annotation { "Feature Type Name" : "Feature", "Feature Type Description" : "" }
export const myFeature = defineFeature(function(context is Context, id is Id, definition is map)
    precondition{}
    {
        {
            var Q0;
            Q0=qCreatedBy(makeId("Front.planeOp"),FACE);
            var sketch = newSketch(context, id + "F0", { "sketchPlane" : qUnion([Q0])});
            skLineSegment(sketch, "E0", {"start": v(-64.1, -46.27) * mm, "end": v(65.9, -46.27) * mm});
            skLineSegment(sketch, "E1", {"start": v(-64.1, -46.27) * mm, "end": v(-64.1, -16.27) * mm});
            skLineSegment(sketch, "E2", {"start": v(-64.1, -46.27) * mm, "end": v(-60.1, -46.27) * mm});
            skLineSegment(sketch, "E3", {"start": v(-60.1, -46.27) * mm, "end": v(-60.1, -16.27) * mm});
            skLineSegment(sketch, "E4", {"start": v(-60.1, -46.27) * mm, "end": v(-53.1, -46.27) * mm});
            skLineSegment(sketch, "E5", {"start": v(-53.1, -46.27) * mm, "end": v(-53.1, -16.27) * mm});
            skLineSegment(sketch, "E6", {"start": v(-49.1, -46.32) * mm, "end": v(-49.1, -16.32) * mm});
            skLineSegment(sketch, "E7", {"start": v(-53.1, -46.32) * mm, "end": v(-49.1, -46.32) * mm});
            skLineSegment(sketch, "E8", {"start": v(-49.1, -46.32) * mm, "end": v(-38.47, -46.27) * mm});
            skLineSegment(sketch, "E9", {"start": v(-38.47, -46.27) * mm, "end": v(-38.89, 32.17) * mm, "construction": true});
            skLineSegment(sketch, "E10", {"start": v(-64.1, -16.27) * mm, "end": v(-60.1, -16.27) * mm});
            skLineSegment(sketch, "E11", {"start": v(-53.1, -16.27) * mm, "end": v(-49.1, -16.32) * mm});
            skLineSegment(sketch, "E12", {"start": v(-68.63, -16.25) * mm, "end": v(-38.63, -16.25) * mm});
            skLineSegment(sketch, "E13", {"start": v(-68.63, -14.09) * mm, "end": v(-38.63, -14.09) * mm});
            skArc(sketch, "E14", {"start": v(-68.63, -14.09) * mm, "mid": v(-69.7, -15.17) * mm, "end": v(-68.63, -16.25) * mm});
            skLineSegment(sketch, "E15", {"start": v(-38.63, -14.09) * mm, "end": v(-38.68, -4.09) * mm});
            skPoint(sketch, "E15.endSnap0", {"position": v(-38.68, -7.05) * mm});
            skLineSegment(sketch, "E16", {"start": v(-38.68, -4.09) * mm, "end": v(-52.68, -4.16) * mm});
            skFitSpline(sketch, "E17", {"points": [v(-52.68, -4.16) * mm, v(-58.68, -8.88) * mm, v(-69.52, -10.67) * mm, v(-80.9, -8.11) * mm, v(-80.17, -8.88) * mm, v(-72.59, -13.73) * mm, v(-68.63, -14.09) * mm], "startDerivative": vector(-32.22, -24.94) * mm, "endDerivative": vector(26.6, -3.14) * mm});
            skLineSegment(sketch, "E18", {"start": v(-38.76, 7.91) * mm, "end": v(-58.76, 7.77) * mm});
            skLineSegment(sketch, "E19", {"start": v(-58.76, 7.77) * mm, "end": v(-52.68, -4.16) * mm});
            skLineSegment(sketch, "E20", {"start": v(-38.76, 7.91) * mm, "end": v(-38.74, 4.91) * mm});
            skLineSegment(sketch, "E21", {"start": v(-38.76, 7.91) * mm, "end": v(-38.9, 32.91) * mm});
            skFitSpline(sketch, "E22", {"points": [v(-38.9, 32.91) * mm, v(-40.61, 19.74) * mm, v(-42.06, 14.37) * mm, v(-43.86, 12.97) * mm, v(-53.8, 12.33) * mm, v(-64.1, 13.48) * mm, v(-69.15, 16.29) * mm, v(-67.17, 13.48) * mm, v(-63.55, 9.39) * mm, v(-58.76, 7.77) * mm], "startDerivative": vector(-10.23, -89.2) * mm, "endDerivative": vector(52.36, -10.93) * mm});
            skPoint(sketch, "E23", {"position": v(-55.8, -6.79) * mm});
            skFitSpline(sketch, "E24", {"points": [v(-55.8, -6.79) * mm, v(-59.58, -4.66) * mm, v(-60.84, -3.51) * mm, v(-58.68, -8.88) * mm], "startDerivative": vector(-11.5, 5.17) * mm, "endDerivative": vector(8.54, -18.92) * mm});
            skPoint(sketch, "E25", {"position": v(-46.92, 12.53) * mm});
            skPoint(sketch, "E26", {"position": v(-51.81, 12.36) * mm});
            skFitSpline(sketch, "E27", {"points": [v(-46.92, 12.53) * mm, v(-50.19, 15.14) * mm, v(-52.72, 17.82) * mm, v(-51.81, 12.36) * mm], "startDerivative": vector(-9.9, 6.4) * mm, "endDerivative": vector(5.44, -21.54) * mm});
            skLineSegment(sketch, "E28.MirrorCS", {"start": v(-23.84, -46.11) * mm, "end": v(-24.16, -16.11) * mm});
            skLineSegment(sketch, "E29.MirrorCS", {"start": v(-27.83, -46.2) * mm, "end": v(-28.15, -16.21) * mm});
            skLineSegment(sketch, "E30.MirrorCS", {"start": v(-16.84, -46.04) * mm, "end": v(-17.16, -16.04) * mm});
            skLineSegment(sketch, "E31.MirrorCS", {"start": v(-12.84, -46) * mm, "end": v(-13.16, -16) * mm});
            skLineSegment(sketch, "E32.MirrorCS", {"start": v(-23.83, -46.17) * mm, "end": v(-27.83, -46.2) * mm});
            skLineSegment(sketch, "E33.MirrorCS", {"start": v(-8.63, -15.93) * mm, "end": v(-38.63, -16.25) * mm});
            skLineSegment(sketch, "E34.MirrorCS", {"start": v(-8.66, -13.77) * mm, "end": v(-38.66, -14.09) * mm});
            skArc(sketch, "E35.MirrorCS", {"start": v(-8.66, -13.77) * mm, "mid": v(-7.57, -14.83) * mm, "end": v(-8.63, -15.93) * mm});
            skFitSpline(sketch, "E36.MirrorCS", {"points": [v(-24.71, -4.01) * mm, v(-18.66, -8.66) * mm, v(-7.8, -10.34) * mm, v(3.55, -7.66) * mm, v(2.83, -8.43) * mm, v(-4.7, -13.37) * mm, v(-8.66, -13.77) * mm], "startDerivative": vector(32.49, -24.6) * mm, "endDerivative": vector(-26.56, -3.42) * mm});
            skFitSpline(sketch, "E37.MirrorCS", {"points": [v(-21.57, -6.6) * mm, v(-17.8, -4.44) * mm, v(-16.55, -3.28) * mm, v(-18.66, -8.66) * mm], "startDerivative": vector(11.44, 5.29) * mm, "endDerivative": vector(-8.33, -19.01) * mm});
            skLineSegment(sketch, "E38.MirrorCS", {"start": v(-38.71, -4.09) * mm, "end": v(-24.71, -4.01) * mm});
            skLineSegment(sketch, "E39.MirrorCS", {"start": v(-18.76, 7.98) * mm, "end": v(-24.71, -4.01) * mm});
            skLineSegment(sketch, "E40.MirrorCS", {"start": v(-38.76, 7.91) * mm, "end": v(-18.76, 7.98) * mm});
            skFitSpline(sketch, "E41.MirrorCS", {"points": [v(-38.9, 32.91) * mm, v(-37.03, 19.75) * mm, v(-35.53, 14.4) * mm, v(-33.7, 13.02) * mm, v(-23.77, 12.49) * mm, v(-13.48, 13.75) * mm, v(-8.46, 16.61) * mm, v(-10.41, 13.78) * mm, v(-13.98, 9.65) * mm, v(-18.76, 7.98) * mm], "startDerivative": vector(11.19, -89.08) * mm, "endDerivative": vector(-52.24, -11.49) * mm});
            skFitSpline(sketch, "E42.MirrorCS", {"points": [v(-30.64, 12.62) * mm, v(-27.4, 15.26) * mm, v(-24.9, 17.97) * mm, v(-25.76, 12.5) * mm], "startDerivative": vector(9.83, 6.51) * mm, "endDerivative": vector(-5.2, -21.6) * mm});
            skLineSegment(sketch, "E43", {"start": v(-16.84, -46.04) * mm, "end": v(-12.84, -46) * mm});
            skLineSegment(sketch, "E44", {"start": v(-16.77, -16.03) * mm, "end": v(-13.16, -16) * mm});
            skLineSegment(sketch, "E45", {"start": v(-28.15, -16.21) * mm, "end": v(-24.16, -16.11) * mm});
            skLineSegment(sketch, "E46", {"start": v(-27.83, -46.2) * mm, "end": v(-23.83, -46.17) * mm});
            skLineSegment(sketch, "E47", {"start": v(-23.83, -46.17) * mm, "end": v(-24.16, -16.11) * mm});
            skLineSegment(sketch, "E48", {"start": v(-28.15, -16.21) * mm, "end": v(-27.83, -46.2) * mm});
            skLineSegment(sketch, "E49", {"start": v(-13.16, -16) * mm, "end": v(-12.84, -46) * mm});
            skLineSegment(sketch, "E50", {"start": v(-16.77, -16.03) * mm, "end": v(-16.84, -46.04) * mm});
            skSolve(sketch);
        }
        {
            var Q0;
            {var subQ5=sQuery(id+"F0.wireOp",EDGE,"E18");Q0=makeQuery(id+"F0.imprint","IMPRINT",FACE,{"disambiguationData":[TD([[makeQuery(id+"F0.imprint","IMPRINT",EDGE,{"derivedFrom":subQ5}),-1.0]])]});}
            var Q1;
            {var subQ0=sQuery(id+"F0.wireOp",EDGE,"E27");Q1=makeQuery(id+"F0.imprint","IMPRINT",FACE,{"disambiguationData":[TD([[makeQuery(id+"F0.imprint","IMPRINT",EDGE,{"derivedFrom":subQ0}),1.0]])]});}
            var Q2;
            {var subQ4=sQuery(id+"F0.wireOp",EDGE,"E21");Q2=makeQuery(id+"F0.imprint","IMPRINT",FACE,{"disambiguationData":[TD([[makeQuery(id+"F0.imprint","IMPRINT",EDGE,{"derivedFrom":subQ4}),-1.0]])]});}
            var Q3;
            {var subQ0=sQuery(id+"F0.wireOp",EDGE,"E42.MirrorCS");Q3=makeQuery(id+"F0.imprint","IMPRINT",FACE,{"disambiguationData":[TD([[makeQuery(id+"F0.imprint","IMPRINT",EDGE,{"derivedFrom":subQ0}),-1.0]])]});}
            var Q4;
            Q4=makeQuery(id+"F0.imprint","IMPRINT",FACE,{"disambiguationData":[TD([[makeQuery(id+"F0.imprint","IMPRINT",EDGE,{"derivedFrom":sQuery(id+"F0.wireOp",EDGE,"E12")}),1.0]])]});
            var Q5;
            {var subQ0=sQuery(id+"F0.wireOp",EDGE,"E37.MirrorCS");var subQ1=sQuery(id+"F0.wireOp",EDGE,"E36.MirrorCS");var subQ2=makeQuery(id+"F0.imprint","INTERSECT",VERTEX,{"disambiguationData":[OD(0.0)],"derivedFrom":[subQ1,subQ0]});Q5=makeQuery(id+"F0.imprint","IMPRINT",FACE,{"disambiguationData":[TD([[makeQuery(id+"F0.imprint","IMPRINT",EDGE,{"disambiguationData":[TD([[subQ2,-1.0]])],"derivedFrom":subQ1}),-1.0]])]});}
            var Q6;
            {var subQ1=sQuery(id+"F0.wireOp",EDGE,"E16");Q6=makeQuery(id+"F0.imprint","IMPRINT",FACE,{"disambiguationData":[TD([[makeQuery(id+"F0.imprint","IMPRINT",EDGE,{"derivedFrom":subQ1}),1.0]])]});}
            var Q7;
            {var subQ0=sQuery(id+"F0.wireOp",EDGE,"E24");Q7=makeQuery(id+"F0.imprint","IMPRINT",FACE,{"disambiguationData":[TD([[makeQuery(id+"F0.imprint","IMPRINT",EDGE,{"derivedFrom":subQ0}),1.0]])]});}
            var Q8;
            {var subQ0=sQuery(id+"F0.wireOp",EDGE,"E37.MirrorCS");Q8=makeQuery(id+"F0.imprint","IMPRINT",FACE,{"disambiguationData":[TD([[makeQuery(id+"F0.imprint","IMPRINT",EDGE,{"derivedFrom":subQ0}),-1.0]])]});}
            var Q9;
            Q9=makeQuery(id+"F0.imprint","IMPRINT",FACE,{"disambiguationData":[TD([[makeQuery(id+"F0.imprint","IMPRINT",EDGE,{"derivedFrom":sQuery(id+"F0.wireOp",EDGE,"E16")}),-1.0]])]});
            var Q10;
            Q10=makeQuery(id+"F0.imprint","IMPRINT",FACE,{"disambiguationData":[TD([[makeQuery(id+"F0.imprint","IMPRINT",EDGE,{"derivedFrom":sQuery(id+"F0.wireOp",EDGE,"E1")}),-1.0]])]});
            var Q11;
            {var subQ0=sQuery(id+"F0.wireOp",EDGE,"E5");Q11=makeQuery(id+"F0.imprint","IMPRINT",FACE,{"disambiguationData":[TD([[makeQuery(id+"F0.imprint","IMPRINT",EDGE,{"derivedFrom":subQ0}),-1.0]])]});}
            var Q12;
            Q12=makeQuery(id+"F0.imprint","IMPRINT",FACE,{"disambiguationData":[TD([[makeQuery(id+"F0.imprint","IMPRINT",EDGE,{"derivedFrom":sQuery(id+"F0.wireOp",EDGE,"E45")}),-1.0]])]});
            var Q13;
            Q13=makeQuery(id+"F0.imprint","IMPRINT",FACE,{"disambiguationData":[TD([[makeQuery(id+"F0.imprint","IMPRINT",EDGE,{"derivedFrom":sQuery(id+"F0.wireOp",EDGE,"E43")}),1.0]])]});
            extrude(context, id + "F1", {"entities" : qUnion([Q0, Q1, Q2, Q3, Q4, Q5, Q6, Q7, Q8, Q9, Q10, Q11, Q12, Q13]), "depth" : 2 * mm});
        }
        {
            var Q0;
            Q0=makeQuery(id+"F1.opExtrude","CAP_FACE",FACE,{"disambiguationData":[OSD([sQuery(id+"F0.wireOp",EDGE,"E12"),sQuery(id+"F0.wireOp",EDGE,"E13"),sQuery(id+"F0.wireOp",EDGE,"E14"),sQuery(id+"F0.wireOp",EDGE,"E15"),sQuery(id+"F0.wireOp",EDGE,"E17"),sQuery(id+"F0.wireOp",EDGE,"E19"),sQuery(id+"F0.wireOp",EDGE,"E22"),sQuery(id+"F0.wireOp",EDGE,"E24"),sQuery(id+"F0.wireOp",EDGE,"E27"),sQuery(id+"F0.wireOp",EDGE,"E34.MirrorCS"),sQuery(id+"F0.wireOp",EDGE,"E35.MirrorCS"),sQuery(id+"F0.wireOp",EDGE,"E33.MirrorCS"),sQuery(id+"F0.wireOp",EDGE,"E36.MirrorCS"),sQuery(id+"F0.wireOp",EDGE,"E37.MirrorCS"),sQuery(id+"F0.wireOp",EDGE,"E39.MirrorCS"),sQuery(id+"F0.wireOp",EDGE,"E41.MirrorCS"),sQuery(id+"F0.wireOp",EDGE,"E42.MirrorCS")])],"isStart":false});
            var sketch = newSketch(context, id + "F2", { "sketchPlane" : qUnion([Q0])});
            skLineSegment(sketch, "E51.bottom", {"start": v(-48.24, 4.53) * mm, "end": v(-29.08, 4.53) * mm});
            skLineSegment(sketch, "E51.top", {"start": v(-48.24, -1.21) * mm, "end": v(-29.08, -1.21) * mm});
            skLineSegment(sketch, "E51.left", {"start": v(-48.24, 4.53) * mm, "end": v(-48.24, -1.21) * mm});
            skLineSegment(sketch, "E51.right", {"start": v(-29.08, 4.53) * mm, "end": v(-29.08, -1.21) * mm});
            skSolve(sketch);
        }
        {
            var Q0;
            Q0=makeQuery(id+"F2.imprint","IMPRINT",FACE,{"disambiguationData":[TD([[makeQuery(id+"F2.imprint","IMPRINT",EDGE,{"derivedFrom":sQuery(id+"F2.wireOp",EDGE,"E51.bottom")}),-1.0]])]});
            extrude(context, id + "F3", {"entities" : qUnion([Q0]), "operationType" : NewBodyOperationType.REMOVE, "oppositeDirection" : true, "depth" : 2 * mm});
        }
        {
            var Q0;
            Q0=qCreatedBy(makeId("Front.planeOp"),FACE);
            var sketch = newSketch(context, id + "F4", { "sketchPlane" : qUnion([Q0])});
            skLineSegment(sketch, "E52", {"start": v(22.14, -46.08) * mm, "end": v(22.14, -17.81) * mm, "construction": true});
            skArc(sketch, "E53", {"start": v(22.14, -28.05) * mm, "mid": v(8.89, -33.25) * mm, "end": v(2.73, -46.08) * mm});
            skArc(sketch, "E54.MirrorCS", {"start": v(22.16, -28.05) * mm, "mid": v(35.42, -33.23) * mm, "end": v(41.6, -46.05) * mm});
            skArc(sketch, "E55", {"start": v(22.14, -22.64) * mm, "mid": v(5.06, -29.4) * mm, "end": v(-2.63, -46.08) * mm});
            skFitSpline(sketch, "E56", {"points": [v(-23.86, -46.08) * mm, v(-9.08, -39.76) * mm, v(5.06, -29.4) * mm], "startDerivative": vector(30.8, 11.19) * mm, "endDerivative": vector(27.03, 22.14) * mm});
            skArc(sketch, "E57.MirrorCS", {"start": v(22.14, -22.64) * mm, "mid": v(39.21, -29.4) * mm, "end": v(46.9, -46.08) * mm});
            skFitSpline(sketch, "E58.MirrorCS", {"points": [v(68.14, -46.08) * mm, v(53.35, -39.76) * mm, v(39.21, -29.4) * mm], "startDerivative": vector(-30.8, 11.19) * mm, "endDerivative": vector(-27.03, 22.14) * mm});
            skArc(sketch, "E59", {"start": v(22.14, -17.81) * mm, "mid": v(11.86, -19.73) * mm, "end": v(3.32, -25.76) * mm});
            skFitSpline(sketch, "E60", {"points": [v(3.32, -25.76) * mm, v(-7.15, -33.81) * mm, v(-18.83, -39.65) * mm], "startDerivative": vector(-20.24, -17.15) * mm, "endDerivative": vector(-24.06, -10.63) * mm});
            skArc(sketch, "E61.MirrorCS", {"start": v(22.14, -17.81) * mm, "mid": v(32.41, -19.73) * mm, "end": v(40.96, -25.76) * mm});
            skFitSpline(sketch, "E62.MirrorCS", {"points": [v(40.96, -25.76) * mm, v(51.43, -33.81) * mm, v(63.1, -39.65) * mm], "startDerivative": vector(20.24, -17.15) * mm, "endDerivative": vector(24.06, -10.63) * mm});
            skLineSegment(sketch, "E63", {"start": v(-18.83, -39.65) * mm, "end": v(-18.83, -35.65) * mm});
            skLineSegment(sketch, "E64", {"start": v(63.1, -39.65) * mm, "end": v(63.1, -35.65) * mm});
            skFitSpline(sketch, "E65", {"points": [v(-18.83, -35.65) * mm, v(-8.47, -29.69) * mm, v(1.8, -22.04) * mm, v(6.43, -17.8) * mm, v(12.47, -14.59) * mm, v(22.14, -13.38) * mm, v(32.8, -14.99) * mm, v(42.88, -22.04) * mm, v(51.13, -29.29) * mm, v(63.1, -35.65) * mm], "startDerivative": vector(85.45, 46.03) * mm, "endDerivative": vector(101.3, -46.93) * mm});
            skLineSegment(sketch, "E66.bottom", {"start": v(-14.67, -26.95) * mm, "end": v(-10.67, -26.95) * mm});
            skLineSegment(sketch, "E66.top", {"start": v(-14.67, -43.45) * mm, "end": v(-10.67, -43.45) * mm});
            skLineSegment(sketch, "E66.left", {"start": v(-14.67, -26.95) * mm, "end": v(-14.67, -43.45) * mm});
            skLineSegment(sketch, "E66.right", {"start": v(-10.67, -26.95) * mm, "end": v(-10.67, -43.45) * mm});
            skLineSegment(sketch, "E67.bottom", {"start": v(-6.15, -22.2) * mm, "end": v(-2.15, -22.2) * mm});
            skLineSegment(sketch, "E67.top", {"start": v(-6.15, -38.7) * mm, "end": v(-2.15, -38.7) * mm});
            skLineSegment(sketch, "E67.left", {"start": v(-6.15, -22.2) * mm, "end": v(-6.15, -38.7) * mm});
            skLineSegment(sketch, "E67.right", {"start": v(-2.15, -22.2) * mm, "end": v(-2.15, -38.7) * mm});
            skLineSegment(sketch, "E68.bottom", {"start": v(2.4, -15.16) * mm, "end": v(6.4, -15.16) * mm});
            skLineSegment(sketch, "E68.top", {"start": v(2.4, -31.66) * mm, "end": v(6.4, -31.66) * mm});
            skLineSegment(sketch, "E68.left", {"start": v(2.4, -15.16) * mm, "end": v(2.4, -31.66) * mm});
            skLineSegment(sketch, "E68.right", {"start": v(6.4, -15.16) * mm, "end": v(6.4, -31.66) * mm});
            skLineSegment(sketch, "E69.bottom", {"start": v(11.15, -10.6) * mm, "end": v(15.15, -10.6) * mm});
            skLineSegment(sketch, "E69.top", {"start": v(11.15, -27.1) * mm, "end": v(15.15, -27.1) * mm});
            skLineSegment(sketch, "E69.left", {"start": v(11.15, -10.6) * mm, "end": v(11.15, -27.1) * mm});
            skLineSegment(sketch, "E69.right", {"start": v(15.15, -10.6) * mm, "end": v(15.15, -27.1) * mm});
            skLineSegment(sketch, "E70.bottom", {"start": v(20.08, -8.13) * mm, "end": v(24.08, -8.13) * mm});
            skLineSegment(sketch, "E70.top", {"start": v(20.08, -24.63) * mm, "end": v(24.08, -24.63) * mm});
            skLineSegment(sketch, "E70.left", {"start": v(20.08, -8.13) * mm, "end": v(20.08, -24.63) * mm});
            skLineSegment(sketch, "E70.right", {"start": v(24.08, -8.13) * mm, "end": v(24.08, -24.63) * mm});
            skLineSegment(sketch, "E71.bottom", {"start": v(37.38, -14.97) * mm, "end": v(41.38, -14.97) * mm});
            skLineSegment(sketch, "E71.top", {"start": v(37.38, -31.47) * mm, "end": v(41.38, -31.47) * mm});
            skLineSegment(sketch, "E71.left", {"start": v(37.38, -14.97) * mm, "end": v(37.38, -31.47) * mm});
            skLineSegment(sketch, "E71.right", {"start": v(41.38, -14.97) * mm, "end": v(41.38, -31.47) * mm});
            skLineSegment(sketch, "E72.bottom", {"start": v(46.12, -22) * mm, "end": v(50.12, -22) * mm});
            skLineSegment(sketch, "E72.top", {"start": v(46.12, -38.5) * mm, "end": v(50.12, -38.5) * mm});
            skLineSegment(sketch, "E72.left", {"start": v(46.12, -22) * mm, "end": v(46.12, -38.5) * mm});
            skLineSegment(sketch, "E72.right", {"start": v(50.12, -22) * mm, "end": v(50.12, -38.5) * mm});
            skLineSegment(sketch, "E73.bottom", {"start": v(29.01, -10.41) * mm, "end": v(33.01, -10.41) * mm});
            skLineSegment(sketch, "E73.top", {"start": v(29.01, -26.91) * mm, "end": v(33.01, -26.91) * mm});
            skLineSegment(sketch, "E73.left", {"start": v(29.01, -10.41) * mm, "end": v(29.01, -26.91) * mm});
            skLineSegment(sketch, "E73.right", {"start": v(33.01, -10.41) * mm, "end": v(33.01, -26.91) * mm});
            skLineSegment(sketch, "E74.bottom", {"start": v(54.3, -26.95) * mm, "end": v(58.3, -26.95) * mm});
            skLineSegment(sketch, "E74.top", {"start": v(54.3, -43.45) * mm, "end": v(58.3, -43.45) * mm});
            skLineSegment(sketch, "E74.left", {"start": v(54.3, -26.95) * mm, "end": v(54.3, -43.45) * mm});
            skLineSegment(sketch, "E74.right", {"start": v(58.3, -26.95) * mm, "end": v(58.3, -43.45) * mm});
            skSolve(sketch);
        }
        {
            var Q0;
            {var subQ0=sQuery(id+"F4.wireOp",EDGE,"E69.left");var subQ1=sQuery(id+"F4.wireOp",EDGE,"E59");var subQ2=makeQuery(id+"F4.imprint","INTERSECT",VERTEX,{"derivedFrom":[subQ1,subQ0]});Q0=makeQuery(id+"F4.imprint","IMPRINT",FACE,{"disambiguationData":[TD([[makeQuery(id+"F4.imprint","IMPRINT",EDGE,{"disambiguationData":[TD([[subQ2,-1.0]])],"derivedFrom":subQ1}),-1.0]])]});}
            var Q1;
            {var subQ5=sQuery(id+"F4.wireOp",EDGE,"E60");var subQ6=sQuery(id+"F4.wireOp",EDGE,"E59");var subQ7=makeQuery(id+"F4.imprint","INTERSECT",VERTEX,{"derivedFrom":[subQ6,subQ5]});Q1=makeQuery(id+"F4.imprint","IMPRINT",FACE,{"disambiguationData":[TD([[makeQuery(id+"F4.imprint","IMPRINT",EDGE,{"disambiguationData":[TD([[subQ7,1.0]])],"derivedFrom":subQ6}),-1.0]])]});}
            var Q2;
            {var subQ5=sQuery(id+"F4.wireOp",EDGE,"E68.bottom");Q2=makeQuery(id+"F4.imprint","IMPRINT",FACE,{"disambiguationData":[TD([[makeQuery(id+"F4.imprint","IMPRINT",EDGE,{"derivedFrom":subQ5}),-1.0]])]});}
            var Q3;
            {var subQ5=sQuery(id+"F4.wireOp",EDGE,"E56");var subQ6=sQuery(id+"F4.wireOp",EDGE,"E55");var subQ7=makeQuery(id+"F4.imprint","INTERSECT",VERTEX,{"derivedFrom":[subQ6,subQ5]});Q3=makeQuery(id+"F4.imprint","IMPRINT",FACE,{"disambiguationData":[TD([[makeQuery(id+"F4.imprint","IMPRINT",EDGE,{"disambiguationData":[TD([[subQ7,1.0]])],"derivedFrom":subQ6}),-1.0]])]});}
            var Q4;
            {var subQ0=sQuery(id+"F4.wireOp",EDGE,"E55");var subQ1=makeQuery(id+"F4.imprint","INTERSECT",VERTEX,{"derivedFrom":[subQ0,sQuery(id+"F4.wireOp",EDGE,"E56")]});Q4=makeQuery(id+"F4.imprint","IMPRINT",FACE,{"disambiguationData":[TD([[makeQuery(id+"F4.imprint","IMPRINT",EDGE,{"disambiguationData":[TD([[subQ1,1.0]])],"derivedFrom":subQ0}),1.0]])]});}
            var Q5;
            {var subQ5=sQuery(id+"F4.wireOp",EDGE,"E67.top");Q5=makeQuery(id+"F4.imprint","IMPRINT",FACE,{"disambiguationData":[TD([[makeQuery(id+"F4.imprint","IMPRINT",EDGE,{"derivedFrom":subQ5}),1.0]])]});}
            var Q6;
            {var subQ0=sQuery(id+"F4.wireOp",EDGE,"E67.left");var subQ1=sQuery(id+"F4.wireOp",EDGE,"E56");var subQ2=makeQuery(id+"F4.imprint","INTERSECT",VERTEX,{"derivedFrom":[subQ1,subQ0]});Q6=makeQuery(id+"F4.imprint","IMPRINT",FACE,{"disambiguationData":[TD([[makeQuery(id+"F4.imprint","IMPRINT",EDGE,{"disambiguationData":[TD([[subQ2,-1.0]])],"derivedFrom":subQ1}),1.0]])]});}
            var Q7;
            {var subQ0=sQuery(id+"F4.wireOp",EDGE,"E68.left");var subQ1=sQuery(id+"F4.wireOp",EDGE,"E60");var subQ2=makeQuery(id+"F4.imprint","INTERSECT",VERTEX,{"derivedFrom":[subQ1,subQ0]});Q7=makeQuery(id+"F4.imprint","IMPRINT",FACE,{"disambiguationData":[TD([[makeQuery(id+"F4.imprint","IMPRINT",EDGE,{"disambiguationData":[TD([[subQ2,-1.0]])],"derivedFrom":subQ1}),-1.0]])]});}
            var Q8;
            {var subQ0=sQuery(id+"F4.wireOp",EDGE,"E67.right");var subQ1=sQuery(id+"F4.wireOp",EDGE,"E60");var subQ2=makeQuery(id+"F4.imprint","INTERSECT",VERTEX,{"derivedFrom":[subQ1,subQ0]});Q8=makeQuery(id+"F4.imprint","IMPRINT",FACE,{"disambiguationData":[TD([[makeQuery(id+"F4.imprint","IMPRINT",EDGE,{"disambiguationData":[TD([[subQ2,-1.0]])],"derivedFrom":subQ1}),-1.0]])]});}
            var Q9;
            {var subQ5=sQuery(id+"F4.wireOp",EDGE,"E67.bottom");Q9=makeQuery(id+"F4.imprint","IMPRINT",FACE,{"disambiguationData":[TD([[makeQuery(id+"F4.imprint","IMPRINT",EDGE,{"derivedFrom":subQ5}),-1.0]])]});}
            var Q10;
            {var subQ0=sQuery(id+"F4.wireOp",EDGE,"E67.left");var subQ1=sQuery(id+"F4.wireOp",EDGE,"E60");var subQ2=makeQuery(id+"F4.imprint","INTERSECT",VERTEX,{"derivedFrom":[subQ1,subQ0]});Q10=makeQuery(id+"F4.imprint","IMPRINT",FACE,{"disambiguationData":[TD([[makeQuery(id+"F4.imprint","IMPRINT",EDGE,{"disambiguationData":[TD([[subQ2,-1.0]])],"derivedFrom":subQ1}),-1.0]])]});}
            var Q11;
            {var subQ0=sQuery(id+"F4.wireOp",EDGE,"E66.left");var subQ1=sQuery(id+"F4.wireOp",EDGE,"E60");var subQ2=makeQuery(id+"F4.imprint","INTERSECT",VERTEX,{"derivedFrom":[subQ1,subQ0]});Q11=makeQuery(id+"F4.imprint","IMPRINT",FACE,{"disambiguationData":[TD([[makeQuery(id+"F4.imprint","IMPRINT",EDGE,{"disambiguationData":[TD([[subQ2,1.0]])],"derivedFrom":subQ1}),-1.0]])]});}
            var Q12;
            {var subQ5=sQuery(id+"F4.wireOp",EDGE,"E66.bottom");Q12=makeQuery(id+"F4.imprint","IMPRINT",FACE,{"disambiguationData":[TD([[makeQuery(id+"F4.imprint","IMPRINT",EDGE,{"derivedFrom":subQ5}),-1.0]])]});}
            var Q13;
            {var subQ5=sQuery(id+"F4.wireOp",EDGE,"E66.top");Q13=makeQuery(id+"F4.imprint","IMPRINT",FACE,{"disambiguationData":[TD([[makeQuery(id+"F4.imprint","IMPRINT",EDGE,{"derivedFrom":subQ5}),1.0]])]});}
            var Q14;
            {var subQ0=sQuery(id+"F4.wireOp",EDGE,"E66.left");var subQ1=sQuery(id+"F4.wireOp",EDGE,"E56");var subQ2=makeQuery(id+"F4.imprint","INTERSECT",VERTEX,{"derivedFrom":[subQ1,subQ0]});Q14=makeQuery(id+"F4.imprint","IMPRINT",FACE,{"disambiguationData":[TD([[makeQuery(id+"F4.imprint","IMPRINT",EDGE,{"disambiguationData":[TD([[subQ2,-1.0]])],"derivedFrom":subQ1}),1.0]])]});}
            var Q15;
            {var subQ0=sQuery(id+"F4.wireOp",EDGE,"E63");Q15=makeQuery(id+"F4.imprint","IMPRINT",FACE,{"disambiguationData":[TD([[makeQuery(id+"F4.imprint","IMPRINT",EDGE,{"derivedFrom":subQ0}),-1.0]])]});}
            var Q16;
            {var subQ0=sQuery(id+"F4.wireOp",EDGE,"E69.right");var subQ1=sQuery(id+"F4.wireOp",EDGE,"E59");var subQ2=makeQuery(id+"F4.imprint","INTERSECT",VERTEX,{"derivedFrom":[subQ1,subQ0]});Q16=makeQuery(id+"F4.imprint","IMPRINT",FACE,{"disambiguationData":[TD([[makeQuery(id+"F4.imprint","IMPRINT",EDGE,{"disambiguationData":[TD([[subQ2,-1.0]])],"derivedFrom":subQ1}),-1.0]])]});}
            var Q17;
            {var subQ0=sQuery(id+"F4.wireOp",EDGE,"E69.right");var subQ1=sQuery(id+"F4.wireOp",EDGE,"E55");var subQ2=makeQuery(id+"F4.imprint","INTERSECT",VERTEX,{"derivedFrom":[subQ1,subQ0]});Q17=makeQuery(id+"F4.imprint","IMPRINT",FACE,{"disambiguationData":[TD([[makeQuery(id+"F4.imprint","IMPRINT",EDGE,{"disambiguationData":[TD([[subQ2,-1.0]])],"derivedFrom":subQ1}),-1.0]])]});}
            var Q18;
            {var subQ5=sQuery(id+"F4.wireOp",EDGE,"E69.bottom");Q18=makeQuery(id+"F4.imprint","IMPRINT",FACE,{"disambiguationData":[TD([[makeQuery(id+"F4.imprint","IMPRINT",EDGE,{"derivedFrom":subQ5}),-1.0]])]});}
            var Q19;
            {var subQ5=sQuery(id+"F4.wireOp",EDGE,"E70.bottom");Q19=makeQuery(id+"F4.imprint","IMPRINT",FACE,{"disambiguationData":[TD([[makeQuery(id+"F4.imprint","IMPRINT",EDGE,{"derivedFrom":subQ5}),-1.0]])]});}
            var Q20;
            {var subQ3=sQuery(id+"F4.wireOp",EDGE,"E59");var subQ7=sQuery(id+"F4.wireOp",EDGE,"E61.MirrorCS");var subQ8=makeQuery(id+"F4.imprint","INTERSECT",VERTEX,{"derivedFrom":[subQ3,subQ7]});Q20=makeQuery(id+"F4.imprint","IMPRINT",FACE,{"disambiguationData":[TD([[makeQuery(id+"F4.imprint","IMPRINT",EDGE,{"disambiguationData":[TD([[subQ8,-1.0]])],"derivedFrom":subQ3}),-1.0]])]});}
            var Q21;
            {var subQ0=sQuery(id+"F4.wireOp",EDGE,"E70.left");var subQ1=sQuery(id+"F4.wireOp",EDGE,"E59");var subQ2=makeQuery(id+"F4.imprint","INTERSECT",VERTEX,{"derivedFrom":[subQ1,subQ0]});Q21=makeQuery(id+"F4.imprint","IMPRINT",FACE,{"disambiguationData":[TD([[makeQuery(id+"F4.imprint","IMPRINT",EDGE,{"disambiguationData":[TD([[subQ2,-1.0]])],"derivedFrom":subQ1}),-1.0]])]});}
            var Q22;
            {var subQ7=sQuery(id+"F4.wireOp",EDGE,"E57.MirrorCS");var subQ8=sQuery(id+"F4.wireOp",EDGE,"E55");var subQ9=makeQuery(id+"F4.imprint","INTERSECT",VERTEX,{"derivedFrom":[subQ8,subQ7]});Q22=makeQuery(id+"F4.imprint","IMPRINT",FACE,{"disambiguationData":[TD([[makeQuery(id+"F4.imprint","IMPRINT",EDGE,{"disambiguationData":[TD([[subQ9,-1.0]])],"derivedFrom":subQ8}),-1.0]])]});}
            var Q23;
            {var subQ1=sQuery(id+"F4.wireOp",EDGE,"E70.top");Q23=makeQuery(id+"F4.imprint","IMPRINT",FACE,{"disambiguationData":[TD([[makeQuery(id+"F4.imprint","IMPRINT",EDGE,{"derivedFrom":subQ1}),1.0]])]});}
            var Q24;
            {var subQ5=sQuery(id+"F4.wireOp",EDGE,"E73.top");Q24=makeQuery(id+"F4.imprint","IMPRINT",FACE,{"disambiguationData":[TD([[makeQuery(id+"F4.imprint","IMPRINT",EDGE,{"derivedFrom":subQ5}),1.0]])]});}
            var Q25;
            {var subQ0=sQuery(id+"F4.wireOp",EDGE,"E73.left");var subQ1=sQuery(id+"F4.wireOp",EDGE,"E57.MirrorCS");var subQ2=makeQuery(id+"F4.imprint","INTERSECT",VERTEX,{"derivedFrom":[subQ1,subQ0]});Q25=makeQuery(id+"F4.imprint","IMPRINT",FACE,{"disambiguationData":[TD([[makeQuery(id+"F4.imprint","IMPRINT",EDGE,{"disambiguationData":[TD([[subQ2,-1.0]])],"derivedFrom":subQ1}),1.0]])]});}
            var Q26;
            {var subQ0=sQuery(id+"F4.wireOp",EDGE,"E73.left");var subQ1=sQuery(id+"F4.wireOp",EDGE,"E61.MirrorCS");var subQ2=makeQuery(id+"F4.imprint","INTERSECT",VERTEX,{"derivedFrom":[subQ1,subQ0]});Q26=makeQuery(id+"F4.imprint","IMPRINT",FACE,{"disambiguationData":[TD([[makeQuery(id+"F4.imprint","IMPRINT",EDGE,{"disambiguationData":[TD([[subQ2,-1.0]])],"derivedFrom":subQ1}),1.0]])]});}
            var Q27;
            {var subQ0=sQuery(id+"F4.wireOp",EDGE,"E70.right");var subQ1=sQuery(id+"F4.wireOp",EDGE,"E61.MirrorCS");var subQ2=makeQuery(id+"F4.imprint","INTERSECT",VERTEX,{"derivedFrom":[subQ1,subQ0]});Q27=makeQuery(id+"F4.imprint","IMPRINT",FACE,{"disambiguationData":[TD([[makeQuery(id+"F4.imprint","IMPRINT",EDGE,{"disambiguationData":[TD([[subQ2,-1.0]])],"derivedFrom":subQ1}),1.0]])]});}
            var Q28;
            {var subQ5=sQuery(id+"F4.wireOp",EDGE,"E73.bottom");Q28=makeQuery(id+"F4.imprint","IMPRINT",FACE,{"disambiguationData":[TD([[makeQuery(id+"F4.imprint","IMPRINT",EDGE,{"derivedFrom":subQ5}),-1.0]])]});}
            var Q29;
            {var subQ0=sQuery(id+"F4.wireOp",EDGE,"E73.right");var subQ1=sQuery(id+"F4.wireOp",EDGE,"E61.MirrorCS");var subQ2=makeQuery(id+"F4.imprint","INTERSECT",VERTEX,{"derivedFrom":[subQ1,subQ0]});Q29=makeQuery(id+"F4.imprint","IMPRINT",FACE,{"disambiguationData":[TD([[makeQuery(id+"F4.imprint","IMPRINT",EDGE,{"disambiguationData":[TD([[subQ2,-1.0]])],"derivedFrom":subQ1}),1.0]])]});}
            var Q30;
            {var subQ3=sQuery(id+"F4.wireOp",EDGE,"E61.MirrorCS");var subQ7=sQuery(id+"F4.wireOp",EDGE,"E62.MirrorCS");var subQ8=makeQuery(id+"F4.imprint","INTERSECT",VERTEX,{"derivedFrom":[subQ3,subQ7]});Q30=makeQuery(id+"F4.imprint","IMPRINT",FACE,{"disambiguationData":[TD([[makeQuery(id+"F4.imprint","IMPRINT",EDGE,{"disambiguationData":[TD([[subQ8,1.0]])],"derivedFrom":subQ3}),1.0]])]});}
            var Q31;
            {var subQ6=sQuery(id+"F4.wireOp",EDGE,"E57.MirrorCS");var subQ9=sQuery(id+"F4.wireOp",EDGE,"E58.MirrorCS");var subQ10=makeQuery(id+"F4.imprint","INTERSECT",VERTEX,{"derivedFrom":[subQ6,subQ9]});Q31=makeQuery(id+"F4.imprint","IMPRINT",FACE,{"disambiguationData":[TD([[makeQuery(id+"F4.imprint","IMPRINT",EDGE,{"disambiguationData":[TD([[subQ10,1.0]])],"derivedFrom":subQ6}),1.0]])]});}
            var Q32;
            {var subQ0=sQuery(id+"F4.wireOp",EDGE,"E57.MirrorCS");var subQ1=makeQuery(id+"F4.imprint","INTERSECT",VERTEX,{"derivedFrom":[subQ0,sQuery(id+"F4.wireOp",EDGE,"E58.MirrorCS")]});Q32=makeQuery(id+"F4.imprint","IMPRINT",FACE,{"disambiguationData":[TD([[makeQuery(id+"F4.imprint","IMPRINT",EDGE,{"disambiguationData":[TD([[subQ1,1.0]])],"derivedFrom":subQ0}),-1.0]])]});}
            var Q33;
            {var subQ5=sQuery(id+"F4.wireOp",EDGE,"E71.bottom");Q33=makeQuery(id+"F4.imprint","IMPRINT",FACE,{"disambiguationData":[TD([[makeQuery(id+"F4.imprint","IMPRINT",EDGE,{"derivedFrom":subQ5}),-1.0]])]});}
            var Q34;
            {var subQ0=sQuery(id+"F4.wireOp",EDGE,"E71.right");var subQ1=sQuery(id+"F4.wireOp",EDGE,"E62.MirrorCS");var subQ2=makeQuery(id+"F4.imprint","INTERSECT",VERTEX,{"derivedFrom":[subQ1,subQ0]});Q34=makeQuery(id+"F4.imprint","IMPRINT",FACE,{"disambiguationData":[TD([[makeQuery(id+"F4.imprint","IMPRINT",EDGE,{"disambiguationData":[TD([[subQ2,-1.0]])],"derivedFrom":subQ1}),1.0]])]});}
            var Q35;
            {var subQ0=sQuery(id+"F4.wireOp",EDGE,"E72.left");var subQ1=sQuery(id+"F4.wireOp",EDGE,"E62.MirrorCS");var subQ2=makeQuery(id+"F4.imprint","INTERSECT",VERTEX,{"derivedFrom":[subQ1,subQ0]});Q35=makeQuery(id+"F4.imprint","IMPRINT",FACE,{"disambiguationData":[TD([[makeQuery(id+"F4.imprint","IMPRINT",EDGE,{"disambiguationData":[TD([[subQ2,-1.0]])],"derivedFrom":subQ1}),1.0]])]});}
            var Q36;
            {var subQ5=sQuery(id+"F4.wireOp",EDGE,"E72.bottom");Q36=makeQuery(id+"F4.imprint","IMPRINT",FACE,{"disambiguationData":[TD([[makeQuery(id+"F4.imprint","IMPRINT",EDGE,{"derivedFrom":subQ5}),-1.0]])]});}
            var Q37;
            {var subQ0=sQuery(id+"F4.wireOp",EDGE,"E72.right");var subQ1=sQuery(id+"F4.wireOp",EDGE,"E58.MirrorCS");var subQ2=makeQuery(id+"F4.imprint","INTERSECT",VERTEX,{"derivedFrom":[subQ1,subQ0]});Q37=makeQuery(id+"F4.imprint","IMPRINT",FACE,{"disambiguationData":[TD([[makeQuery(id+"F4.imprint","IMPRINT",EDGE,{"disambiguationData":[TD([[subQ2,-1.0]])],"derivedFrom":subQ1}),-1.0]])]});}
            var Q38;
            {var subQ5=sQuery(id+"F4.wireOp",EDGE,"E72.top");Q38=makeQuery(id+"F4.imprint","IMPRINT",FACE,{"disambiguationData":[TD([[makeQuery(id+"F4.imprint","IMPRINT",EDGE,{"derivedFrom":subQ5}),1.0]])]});}
            var Q39;
            {var subQ0=sQuery(id+"F4.wireOp",EDGE,"E72.right");var subQ1=sQuery(id+"F4.wireOp",EDGE,"E62.MirrorCS");var subQ2=makeQuery(id+"F4.imprint","INTERSECT",VERTEX,{"derivedFrom":[subQ1,subQ0]});Q39=makeQuery(id+"F4.imprint","IMPRINT",FACE,{"disambiguationData":[TD([[makeQuery(id+"F4.imprint","IMPRINT",EDGE,{"disambiguationData":[TD([[subQ2,-1.0]])],"derivedFrom":subQ1}),1.0]])]});}
            var Q40;
            {var subQ0=sQuery(id+"F4.wireOp",EDGE,"E74.right");var subQ1=sQuery(id+"F4.wireOp",EDGE,"E62.MirrorCS");var subQ2=makeQuery(id+"F4.imprint","INTERSECT",VERTEX,{"derivedFrom":[subQ1,subQ0]});Q40=makeQuery(id+"F4.imprint","IMPRINT",FACE,{"disambiguationData":[TD([[makeQuery(id+"F4.imprint","IMPRINT",EDGE,{"disambiguationData":[TD([[subQ2,1.0]])],"derivedFrom":subQ1}),1.0]])]});}
            var Q41;
            {var subQ5=sQuery(id+"F4.wireOp",EDGE,"E74.bottom");Q41=makeQuery(id+"F4.imprint","IMPRINT",FACE,{"disambiguationData":[TD([[makeQuery(id+"F4.imprint","IMPRINT",EDGE,{"derivedFrom":subQ5}),-1.0]])]});}
            var Q42;
            {var subQ0=sQuery(id+"F4.wireOp",EDGE,"E74.right");var subQ1=sQuery(id+"F4.wireOp",EDGE,"E58.MirrorCS");var subQ2=makeQuery(id+"F4.imprint","INTERSECT",VERTEX,{"derivedFrom":[subQ1,subQ0]});Q42=makeQuery(id+"F4.imprint","IMPRINT",FACE,{"disambiguationData":[TD([[makeQuery(id+"F4.imprint","IMPRINT",EDGE,{"disambiguationData":[TD([[subQ2,-1.0]])],"derivedFrom":subQ1}),-1.0]])]});}
            var Q43;
            {var subQ5=sQuery(id+"F4.wireOp",EDGE,"E74.top");Q43=makeQuery(id+"F4.imprint","IMPRINT",FACE,{"disambiguationData":[TD([[makeQuery(id+"F4.imprint","IMPRINT",EDGE,{"derivedFrom":subQ5}),1.0]])]});}
            var Q44;
            {var subQ0=sQuery(id+"F4.wireOp",EDGE,"E64");Q44=makeQuery(id+"F4.imprint","IMPRINT",FACE,{"disambiguationData":[TD([[makeQuery(id+"F4.imprint","IMPRINT",EDGE,{"derivedFrom":subQ0}),1.0]])]});}
            var Q45;
            {var subQ5=sQuery(id+"F4.wireOp",EDGE,"E69.top");Q45=makeQuery(id+"F4.imprint","IMPRINT",FACE,{"disambiguationData":[TD([[makeQuery(id+"F4.imprint","IMPRINT",EDGE,{"derivedFrom":subQ5}),1.0]])]});}
            extrude(context, id + "F5", {"entities" : qUnion([Q0, Q1, Q2, Q3, Q4, Q5, Q6, Q7, Q8, Q9, Q10, Q11, Q12, Q13, Q14, Q15, Q16, Q17, Q18, Q19, Q20, Q21, Q22, Q23, Q24, Q25, Q26, Q27, Q28, Q29, Q30, Q31, Q32, Q33, Q34, Q35, Q36, Q37, Q38, Q39, Q40, Q41, Q42, Q43, Q44, Q45]), "operationType" : NewBodyOperationType.ADD, "depth" : 2 * mm});
        }
        {
            var Q0;
            Q0=qCreatedBy(makeId("Front.planeOp"),FACE);
            var sketch = newSketch(context, id + "F6", { "sketchPlane" : qUnion([Q0])});
            skArc(sketch, "E75", {"start": v(41.3, -46.18) * mm, "mid": v(21.97, -27.85) * mm, "end": v(2.64, -46.18) * mm});
            skArc(sketch, "E76", {"start": v(46.94, -46.18) * mm, "mid": v(22.07, -22.61) * mm, "end": v(-2.8, -46.18) * mm});
            skFitSpline(sketch, "E77", {"points": [v(4.68, -29.7) * mm, v(-9.04, -39.94) * mm, v(-23.74, -46.18) * mm], "startDerivative": vector(-26.25, -22) * mm, "endDerivative": vector(-30.64, -10.89) * mm});
            skFitSpline(sketch, "E78", {"points": [v(39.26, -29.5) * mm, v(52.98, -39.54) * mm, v(68.09, -46.18) * mm], "startDerivative": vector(26.47, -21.54) * mm, "endDerivative": vector(31.22, -11.78) * mm});
            skLineSegment(sketch, "E79", {"start": v(-23.74, -46.18) * mm, "end": v(-2.8, -46.18) * mm});
            skLineSegment(sketch, "E80", {"start": v(-2.8, -46.18) * mm, "end": v(2.64, -46.18) * mm});
            skLineSegment(sketch, "E81", {"start": v(41.3, -46.18) * mm, "end": v(46.94, -46.18) * mm});
            skLineSegment(sketch, "E82", {"start": v(46.94, -46.18) * mm, "end": v(68.09, -46.18) * mm});
            skSolve(sketch);
        }
        {
            var Q0;
            {var subQ2=sQuery(id+"F6.wireOp",EDGE,"E77");Q0=makeQuery(id+"F6.imprint","IMPRINT",FACE,{"disambiguationData":[TD([[makeQuery(id+"F6.imprint","IMPRINT",EDGE,{"derivedFrom":subQ2}),1.0]])]});}
            var Q1;
            Q1=makeQuery(id+"F6.imprint","IMPRINT",FACE,{"disambiguationData":[TD([[makeQuery(id+"F6.imprint","IMPRINT",EDGE,{"derivedFrom":sQuery(id+"F6.wireOp",EDGE,"E75")}),-1.0]])]});
            var Q2;
            {var subQ2=sQuery(id+"F6.wireOp",EDGE,"E78");Q2=makeQuery(id+"F6.imprint","IMPRINT",FACE,{"disambiguationData":[TD([[makeQuery(id+"F6.imprint","IMPRINT",EDGE,{"derivedFrom":subQ2}),-1.0]])]});}
            extrude(context, id + "F7", {"entities" : qUnion([Q0, Q1, Q2]), "depth" : 2 * mm});
        }
        {
            var Q0;
            Q0=qCreatedBy(makeId("Front.planeOp"),FACE);
            var sketch = newSketch(context, id + "F8", { "sketchPlane" : qUnion([Q0])});
            skFitSpline(sketch, "E83", {"points": [v(-48.64, 28.61) * mm, v(-40.33, 26.46) * mm, v(-29.87, 27.7) * mm, v(-23.1, 30.15) * mm, v(-7.7, 27.08) * mm, v(7.07, 26.77) * mm, v(8.6, 26.46) * mm, v(16.3, 25.54) * mm, v(26.76, 28.61) * mm, v(32.3, 36.92) * mm, v(31.69, 48.31) * mm, v(22.46, 56.32) * mm, v(9.84, 54.47) * mm, v(6.76, 42.77) * mm, v(15.38, 38.77) * mm, v(21.53, 44.62) * mm, v(18.15, 49.24) * mm, v(13.84, 45.54) * mm, v(15.07, 51.4) * mm, v(21.53, 52) * mm, v(26.46, 47.7) * mm, v(27.07, 38.46) * mm, v(20.6, 32.3) * mm, v(9.84, 32.3) * mm, v(5.84, 34.77) * mm, v(3.07, 32.3) * mm, v(-5.55, 32.62) * mm, v(-13.86, 36) * mm, v(-16.63, 45.85) * mm, v(-10.48, 55.08) * mm, v(3.07, 57.24) * mm, v(2.76, 58.78) * mm, v(3.68, 65.55) * mm, v(12, 70.47) * mm, v(24, 69.86) * mm, v(30.77, 64.32) * mm, v(31.69, 56.93) * mm, v(34.46, 57.55) * mm, v(42.15, 55.08) * mm, v(45.54, 44.62) * mm, v(41.85, 33.23) * mm, v(35.38, 28) * mm, v(34.77, 25.84) * mm, v(32.3, 22.46) * mm, v(25.53, 19.07) * mm, v(10.76, 19.69) * mm, v(6.45, 21.23) * mm, v(-4.94, 20) * mm, v(-21.56, 24.92) * mm, v(-29.87, 22.46) * mm, v(-43.72, 22.46) * mm, v(-48.64, 28.61) * mm]});
            skSolve(sketch);
        }
        {
            var Q0;
            Q0 = qSketchRegion(id + "F8", true);
            extrude(context, id + "F9", {"entities" : qUnion([Q0]), "operationType" : NewBodyOperationType.ADD, "depth" : 2 * mm});
        }
        {
            var Q0;
            Q0=qCreatedBy(makeId("Right.planeOp"),FACE);
            cPlane(context, id + "F10", {"entities" : qUnion([Q0]), "cplaneType" : CPlaneType.OFFSET, "offset" : 90 * mm, "oppositeDirection" : true, "width" : 150 * mm, "height" : 150 * mm});
        }
        {
            var Q0;
            Q0=qCreatedBy(id+"F10.planeOp",FACE);
            var sketch = newSketch(context, id + "F11", { "sketchPlane" : qUnion([Q0])});
            skLineSegment(sketch, "E84", {"start": v(108.26, 5.08) * mm, "end": v(-15.98, -52.66) * mm});
            skLineSegment(sketch, "E85", {"start": v(108.26, 5.08) * mm, "end": v(109.1, 3.26) * mm});
            skLineSegment(sketch, "E86", {"start": v(-15.98, -52.66) * mm, "end": v(-15.14, -54.48) * mm});
            skLineSegment(sketch, "E87", {"start": v(109.1, 3.26) * mm, "end": v(-15.14, -54.48) * mm});
            skPoint(sketch, "E88", {"position": v(-2.85, -46.56) * mm});
            skSolve(sketch);
        }
        {
            var Q0;
            Q0 = qSketchRegion(id + "F11", true);
            extrude(context, id + "F12", {"entities" : qUnion([Q0]), "depth" : 165 * mm});
        }
        {
            var Q0;
            Q0=makeQuery(id+"F12.opExtrude","SWEPT_FACE",FACE,{"disambiguationData":[OSD([sQuery(id+"F11.wireOp",EDGE,"E87")])]});
            var sketch = newSketch(context, id + "F13", { "sketchPlane" : qUnion([Q0])});
            skLineSegment(sketch, "E89", {"start": v(-63.99, 23.13) * mm, "end": v(-63.99, -6.74) * mm});
            skLineSegment(sketch, "E90", {"start": v(-63.99, -6.74) * mm, "end": v(-67.9, -6.74) * mm});
            skLineSegment(sketch, "E91", {"start": v(-63.99, 23.13) * mm, "end": v(-59.73, 23.13) * mm});
            skLineSegment(sketch, "E92", {"start": v(-59.73, 23.13) * mm, "end": v(-59.73, -6.82) * mm});
            skLineSegment(sketch, "E93", {"start": v(-59.73, -6.82) * mm, "end": v(-53.08, -6.82) * mm});
            skLineSegment(sketch, "E94", {"start": v(-53.08, -6.82) * mm, "end": v(-53.08, 23.4) * mm});
            skLineSegment(sketch, "E95", {"start": v(-53.08, 23.4) * mm, "end": v(-48.9, 23.4) * mm});
            skLineSegment(sketch, "E96", {"start": v(-48.9, 23.4) * mm, "end": v(-48.9, -6.98) * mm});
            skLineSegment(sketch, "E97", {"start": v(-48.9, -6.98) * mm, "end": v(-27.8, -6.98) * mm});
            skLineSegment(sketch, "E98", {"start": v(-27.8, -6.98) * mm, "end": v(-27.8, 22.83) * mm});
            skArc(sketch, "E99", {"start": v(3.18, 22.83) * mm, "mid": v(9.29, 9.9) * mm, "end": v(22.6, 4.7) * mm});
            skArc(sketch, "E100", {"start": v(22.6, 4.7) * mm, "mid": v(35.9, 10.06) * mm, "end": v(41.94, 23.07) * mm});
            skLineSegment(sketch, "E101", {"start": v(41.94, 23.07) * mm, "end": v(68.4, 23.07) * mm});
            skLineSegment(sketch, "E102", {"start": v(54.84, 7.98) * mm, "end": v(54.84, 3.83) * mm});
            skLineSegment(sketch, "E103", {"start": v(54.84, 3.83) * mm, "end": v(58.77, 3.83) * mm});
            skLineSegment(sketch, "E104", {"start": v(58.77, 3.83) * mm, "end": v(58.77, 9.95) * mm});
            skFitSpline(sketch, "E105", {"points": [v(58.77, 9.95) * mm, v(61.4, 11.48) * mm, v(63.58, 12.35) * mm], "startDerivative": vector(5, 3.15) * mm, "endDerivative": vector(4.6, 1.63) * mm});
            skLineSegment(sketch, "E106", {"start": v(63.58, 12.35) * mm, "end": v(63.58, 16.5) * mm});
            skLineSegment(sketch, "E107", {"start": v(58.77, 14.1) * mm, "end": v(58.77, 19.13) * mm});
            skFitSpline(sketch, "E108", {"points": [v(58.77, 14.1) * mm, v(61.18, 15.41) * mm, v(63.58, 16.5) * mm], "startDerivative": vector(4.74, 2.7) * mm, "endDerivative": vector(4.87, 2.1) * mm});
            skFitSpline(sketch, "E109", {"points": [v(58.77, 19.13) * mm, v(62.7, 21.1) * mm, v(68.4, 23.07) * mm], "startDerivative": vector(8.07, 4.41) * mm, "endDerivative": vector(11.09, 3.48) * mm});
            skLineSegment(sketch, "E110", {"start": v(-23.95, -6.98) * mm, "end": v(-23.95, 22.83) * mm});
            skLineSegment(sketch, "E111", {"start": v(-23.95, -6.98) * mm, "end": v(-16.77, -6.98) * mm});
            skLineSegment(sketch, "E112", {"start": v(-16.77, -6.98) * mm, "end": v(-16.77, 11.4) * mm});
            skLineSegment(sketch, "E113", {"start": v(-16.77, 11.4) * mm, "end": v(-18.5, 12.58) * mm});
            skLineSegment(sketch, "E114", {"start": v(-18.5, 12.58) * mm, "end": v(-18.5, 16.76) * mm});
            skLineSegment(sketch, "E115", {"start": v(-18.5, 16.76) * mm, "end": v(-16.77, 15.56) * mm});
            skLineSegment(sketch, "E116", {"start": v(-16.77, 15.56) * mm, "end": v(-16.77, 20.31) * mm});
            skLineSegment(sketch, "E117", {"start": v(-12.9, -7.1) * mm, "end": v(-8.55, -7.1) * mm});
            skLineSegment(sketch, "E118", {"start": v(-12.9, -7.1) * mm, "end": v(-12.9, 3.81) * mm});
            skLineSegment(sketch, "E119", {"start": v(-12.9, 3.81) * mm, "end": v(-10.33, 3.81) * mm});
            skLineSegment(sketch, "E120", {"start": v(-10.33, 3.81) * mm, "end": v(-10.33, 7.74) * mm});
            skFitSpline(sketch, "E121", {"points": [v(-10.33, 7.74) * mm, v(-8.27, 6.48) * mm, v(-5.8, 4.96) * mm], "startDerivative": vector(4.22, -2.6) * mm, "endDerivative": vector(4.85, -2.96) * mm});
            skLineSegment(sketch, "E122", {"start": v(-5.8, 4.96) * mm, "end": v(-5.8, -0.96) * mm});
            skLineSegment(sketch, "E123", {"start": v(-5.8, -0.96) * mm, "end": v(-1.85, -0.96) * mm});
            skLineSegment(sketch, "E124", {"start": v(-1.85, -0.96) * mm, "end": v(-1.85, 1.8) * mm});
            skLineSegment(sketch, "E125", {"start": v(2.81, -1.86) * mm, "end": v(2.81, -7.98) * mm});
            skLineSegment(sketch, "E126", {"start": v(2.81, -7.98) * mm, "end": v(6.74, -7.98) * mm});
            skLineSegment(sketch, "E127", {"start": v(6.74, -7.98) * mm, "end": v(6.74, -5.3) * mm});
            skPoint(sketch, "E128.startSnap0", {"position": v(54.84, 5.9) * mm});
            skFitSpline(sketch, "E129", {"points": [v(54.84, 7.98) * mm, v(50.86, 5.9) * mm], "startDerivative": vector(-3.98, -2.08) * mm, "endDerivative": vector(-3.98, -2.08) * mm});
            skLineSegment(sketch, "E130", {"start": v(50.86, 5.9) * mm, "end": v(50.86, -1.24) * mm});
            skLineSegment(sketch, "E131", {"start": v(50.86, -1.24) * mm, "end": v(46.56, -1.24) * mm});
            skLineSegment(sketch, "E132", {"start": v(46.56, -1.24) * mm, "end": v(46.56, 2.12) * mm});
            skLineSegment(sketch, "E133", {"start": v(41.85, -2.42) * mm, "end": v(41.85, -8.47) * mm});
            skLineSegment(sketch, "E134", {"start": v(41.85, -8.47) * mm, "end": v(37.9, -8.47) * mm});
            skLineSegment(sketch, "E135", {"start": v(37.9, -8.47) * mm, "end": v(37.9, -5.53) * mm});
            skLineSegment(sketch, "E136", {"start": v(33.35, -8.19) * mm, "end": v(33.35, -12.98) * mm});
            skLineSegment(sketch, "E137", {"start": v(33.35, -12.98) * mm, "end": v(29.45, -12.98) * mm});
            skLineSegment(sketch, "E138", {"start": v(29.45, -12.98) * mm, "end": v(29.45, -9.39) * mm});
            skLineSegment(sketch, "E139", {"start": v(24.55, -9.99) * mm, "end": v(24.55, -15.18) * mm});
            skLineSegment(sketch, "E140", {"start": v(24.55, -15.18) * mm, "end": v(20.56, -15.18) * mm});
            skLineSegment(sketch, "E141", {"start": v(20.56, -15.18) * mm, "end": v(20.56, -9.89) * mm});
            skLineSegment(sketch, "E142", {"start": v(15.66, -9.29) * mm, "end": v(15.66, -12.78) * mm});
            skLineSegment(sketch, "E143", {"start": v(15.66, -12.78) * mm, "end": v(11.56, -12.78) * mm});
            skLineSegment(sketch, "E144", {"start": v(11.56, -12.78) * mm, "end": v(11.56, -8.09) * mm});
            skFitSpline(sketch, "E145", {"points": [v(46.56, 2.12) * mm, v(44.14, 0) * mm, v(41.85, -2.42) * mm], "startDerivative": vector(-4.96, -4.15) * mm, "endDerivative": vector(-4.45, -4.92) * mm});
            skFitSpline(sketch, "E146", {"points": [v(37.9, -5.53) * mm, v(35.45, -6.99) * mm, v(33.35, -8.19) * mm], "startDerivative": vector(-4.8, -2.89) * mm, "endDerivative": vector(-4.3, -2.43) * mm});
            skFitSpline(sketch, "E147", {"points": [v(24.55, -9.99) * mm, v(29.45, -9.39) * mm], "startDerivative": vector(4.9, 0.6) * mm, "endDerivative": vector(4.9, 0.6) * mm});
            skFitSpline(sketch, "E148", {"points": [v(20.56, -9.89) * mm, v(17.86, -9.89) * mm, v(15.66, -9.29) * mm], "startDerivative": vector(-5.33, -0.33) * mm, "endDerivative": vector(-4.45, 1.55) * mm});
            skFitSpline(sketch, "E149", {"points": [v(11.56, -8.09) * mm, v(8.56, -6.49) * mm, v(6.74, -5.3) * mm], "startDerivative": vector(-5.76, 2.94) * mm, "endDerivative": vector(-3.82, 2.63) * mm});
            skFitSpline(sketch, "E150", {"points": [v(2.81, -1.86) * mm, v(-1.85, 1.8) * mm], "startDerivative": vector(-4.66, 3.65) * mm, "endDerivative": vector(-4.66, 3.65) * mm});
            skArc(sketch, "E151", {"start": v(-8.55, -9.35) * mm, "mid": v(-7.43, -8.23) * mm, "end": v(-8.55, -7.1) * mm});
            skFitSpline(sketch, "E152", {"points": [v(-8.55, -9.35) * mm, v(-5.94, -9.35) * mm, v(-4.62, -9.76) * mm, v(-1.65, -11.17) * mm, v(3.16, -14.85) * mm, v(3.73, -15.51) * mm, v(1.65, -14.95) * mm, v(-6.13, -13.06) * mm, v(-9.76, -12.59) * mm, v(-13.02, -12.63) * mm, v(-17.73, -14) * mm, v(-18.44, -14.47) * mm, v(-18.16, -15.18) * mm, v(-16.93, -17.96) * mm, v(-16.32, -19.76) * mm, v(-17.36, -18.9) * mm, v(-19.67, -17.4) * mm, v(-21.37, -16.55) * mm, v(-21.6, -16.74) * mm, v(-24.43, -19.05) * mm], "startDerivative": vector(53.27, 2.74) * mm, "endDerivative": vector(-57.89, -44.55) * mm});
            skLineSegment(sketch, "E153", {"start": v(-24.43, -19.05) * mm, "end": v(-18.62, -31.15) * mm});
            skFitSpline(sketch, "E154", {"points": [v(-18.62, -31.15) * mm, v(-15.83, -31.9) * mm, v(-13.59, -33.02) * mm, v(-10.07, -37.22) * mm, v(-8.42, -39.61) * mm, v(-9.77, -38.86) * mm, v(-13.21, -36.84) * mm, v(-16.58, -35.94) * mm], "startDerivative": vector(21.2, -5.4) * mm, "endDerivative": vector(-22.48, 4.25) * mm});
            skFitSpline(sketch, "E155", {"points": [v(-16.58, -35.94) * mm, v(-20.77, -35.35) * mm, v(-25.64, -35.35) * mm, v(-25.5, -35.94) * mm, v(-24.52, -39.54) * mm, v(-24.82, -41.26) * mm, v(-26.09, -39.61) * mm, v(-28.19, -37.37) * mm, v(-30.66, -35.94) * mm, v(-32.45, -35.94) * mm, v(-34.77, -36.92) * mm, v(-36.5, -41.4) * mm, v(-36.65, -42.08) * mm, v(-35.9, -42.08) * mm, v(-31.18, -43.13) * mm, v(-26.91, -45.23) * mm, v(-23.24, -46.05) * mm, v(-19.35, -45.15) * mm, v(-12.54, -42.6) * mm, v(-7.97, -41.33) * mm, v(-4.9, -41.11) * mm, v(-2.58, -40.96) * mm, v(2.5, -41.93) * mm, v(5.73, -42.23) * mm, v(8.65, -40.96) * mm, v(13.96, -39.76) * mm, v(22.56, -39.64) * mm, v(27.27, -40.88) * mm, v(31.09, -43.12) * mm, v(33.67, -46.49) * mm, v(34.45, -49.18) * mm, v(35.57, -49.96) * mm, v(40.28, -53.55) * mm, v(44.21, -60.4) * mm, v(44.1, -70.83) * mm, v(40.59, -76.69) * mm, v(35.12, -78.76) * mm, v(32.29, -78.2) * mm, v(31.15, -77.73) * mm, v(30.4, -78.1) * mm, v(30.3, -79.14) * mm, v(29.83, -85.56) * mm, v(25.21, -89.99) * mm, v(17.2, -91.88) * mm, v(8.61, -90.93) * mm, v(3.14, -87.16) * mm, v(1.25, -83.39) * mm, v(2, -78.48) * mm, v(1.63, -78) * mm, v(-2.52, -77.54) * mm, v(-9.22, -76.78) * mm, v(-14.88, -74.24) * mm, v(-17.8, -67.07) * mm, v(-17.52, -61.7) * mm, v(-15.73, -58.1) * mm, v(-13.27, -55.75) * mm, v(-4.6, -53.2) * mm, v(-0.73, -52.73) * mm, v(2.38, -53.3) * mm, v(4.55, -55.65) * mm, v(7.1, -54.52) * mm, v(8.7, -53.3) * mm, v(12.48, -52.26) * mm, v(16.91, -52.54) * mm, v(22.29, -54.24) * mm, v(26.06, -59.62) * mm, v(25.3, -68.76) * mm, v(20.68, -72.92) * mm, v(16.25, -73.76) * mm, v(14.08, -72.16) * mm, v(12.67, -70.27) * mm, v(12.67, -66.4) * mm, v(13.7, -67.07) * mm, v(15.78, -69.7) * mm, v(17.85, -70) * mm, v(18.6, -69.7) * mm, v(20.12, -67.63) * mm, v(20.3, -64.52) * mm, v(17.29, -60.75) * mm, v(12.48, -59.7) * mm, v(7.86, -60.84) * mm, v(5.03, -65.84) * mm, v(6.63, -72.92) * mm, v(11.82, -77.35) * mm, v(21.44, -77.16) * mm, v(30.59, -69.52) * mm, v(31.44, -57.92) * mm, v(25.68, -49.43) * mm, v(15.5, -46.4) * mm, v(7.45, -47.47) * mm, v(6.18, -47.79) * mm, v(-8.54, -48) * mm, v(-23.9, -50.96) * mm, v(-30.88, -48.42) * mm, v(-37.44, -46.94) * mm, v(-37.44, -48.1) * mm, v(-37.66, -48.84) * mm, v(-38.6, -55.94) * mm, v(-39.14, -52.97) * mm, v(-39.88, -47.04) * mm, v(-40.4, -47.26) * mm, v(-43.06, -47.79) * mm, v(-48.77, -49.7) * mm, v(-49.52, -49.8) * mm, v(-49.2, -47.47) * mm, v(-44.54, -43.34) * mm, v(-40.52, -42.17) * mm], "startDerivative": vector(-387.3, 68.23) * mm, "endDerivative": vector(413.25, 72.6) * mm});
            skFitSpline(sketch, "E156", {"points": [v(-40.52, -42.17) * mm, v(-41.7, -37.7) * mm, v(-43.5, -36.01) * mm, v(-46.67, -35.6) * mm, v(-47.2, -35.8) * mm, v(-50.06, -38.45) * mm, v(-52.5, -40.78) * mm, v(-52.28, -38.87) * mm, v(-51.44, -35.6) * mm, v(-52.81, -35.49) * mm, v(-55.78, -35.38) * mm, v(-62.13, -36.01) * mm, v(-68.9, -39.5) * mm, v(-68.06, -37.7) * mm, v(-65.1, -34.21) * mm, v(-61.28, -31.25) * mm, v(-58.74, -31.04) * mm, v(-58.95, -31.04) * mm], "startDerivative": vector(-13.19, 68.18) * mm, "endDerivative": vector(-20.68, 0.47) * mm});
            skLineSegment(sketch, "E157", {"start": v(-58.74, -31.04) * mm, "end": v(-52.7, -18.97) * mm});
            skArc(sketch, "E158", {"start": v(-67.9, -6.74) * mm, "mid": v(-69.57, -7.98) * mm, "end": v(-67.9, -9.23) * mm});
            skFitSpline(sketch, "E159", {"points": [v(-67.9, -9.23) * mm, v(-73.88, -10.4) * mm, v(-80.66, -14.63) * mm, v(-77.38, -13.89) * mm, v(-68.9, -12.3) * mm, v(-61.28, -13.04) * mm, v(-58.53, -14.3) * mm, v(-59.17, -15.37) * mm, v(-60.75, -19.82) * mm, v(-59.59, -18.65) * mm, v(-55.78, -16.43) * mm, v(-55.35, -16.32) * mm, v(-52.7, -18.97) * mm], "startDerivative": vector(-50.26, -1.5) * mm, "endDerivative": vector(40.86, -45.54) * mm});
            skLineSegment(sketch, "E160", {"start": v(-23.95, 22.83) * mm, "end": v(-27.8, 22.83) * mm});
            skLineSegment(sketch, "E161", {"start": v(3.18, 22.83) * mm, "end": v(-20.82, 22.83) * mm});
            skLineSegment(sketch, "E162", {"start": v(-20.82, 22.83) * mm, "end": v(-16.77, 20.31) * mm});
            skSolve(sketch);
        }
        {
            var Q0;
            Q0 = qSketchRegion(id + "F13", true);
            extrude(context, id + "F14", {"entities" : qUnion([Q0]), "operationType" : NewBodyOperationType.REMOVE, "oppositeDirection" : true, "depth" : 4 * mm});
        }
        {
            var Q0;
            Q0=qCreatedBy(id+"F10.planeOp",FACE);
            var sketch = newSketch(context, id + "F15", { "sketchPlane" : qUnion([Q0])});
            skLineSegment(sketch, "E163", {"start": v(-16.05, -52.8) * mm, "end": v(-16.05, -37.8) * mm});
            skLineSegment(sketch, "E164", {"start": v(-16.05, -37.8) * mm, "end": v(-18.05, -37.8) * mm});
            skLineSegment(sketch, "E165", {"start": v(-18.05, -37.8) * mm, "end": v(-18.05, -54.31) * mm});
            skLineSegment(sketch, "E166", {"start": v(-16.05, -52.8) * mm, "end": v(-14.02, -52.8) * mm});
            skLineSegment(sketch, "E167", {"start": v(-14.02, -52.8) * mm, "end": v(-14.34, -54.1) * mm});
            skLineSegment(sketch, "E168", {"start": v(-14.34, -54.1) * mm, "end": v(-16.4, -55.1) * mm});
            skArc(sketch, "E169", {"start": v(-18.05, -54.31) * mm, "mid": v(-17.47, -55.23) * mm, "end": v(-16.4, -55.1) * mm});
            skSolve(sketch);
        }
        {
            var Q0;
            Q0 = qSketchRegion(id + "F15", true);
            extrude(context, id + "F16", {"entities" : qUnion([Q0]), "operationType" : NewBodyOperationType.ADD, "depth" : 165 * mm});
        }
        {
            var Q0;
            Q0=makeQuery(id+"F16.opExtrude","SWEPT_EDGE",EDGE,{"disambiguationData":[OSD([sQuery(id+"F15.wireOp",EDGE,"E164"),sQuery(id+"F15.wireOp",EDGE,"E165")])]});
            fillet(context, id + "F17", {"entities" : qUnion([Q0]), "radius" : 5 * mm, "tangentPropagation" : true, "allowEdgeOverflow" : false});
        }
        {
            var Q0;
            Q0=makeQuery(id+"F16.opExtrude","SWEPT_FACE",FACE,{"disambiguationData":[OSD([sQuery(id+"F15.wireOp",EDGE,"E165")])]});
            var sketch = newSketch(context, id + "F18", { "sketchPlane" : qUnion([Q0])});
            skText(sketch, "E170", { "text": "Fang Yiran", "fontName": "OpenSans-Bold.ttf"});
            skArc(sketch, "E171", {"start": v(-68.99, -52) * mm, "mid": v(-77.72, -43.2) * mm, "end": v(-86.45, -52) * mm});
            skArc(sketch, "E172", {"start": v(-53.46, -52) * mm, "mid": v(-61.22, -44.23) * mm, "end": v(-68.99, -52) * mm});
            skArc(sketch, "E173", {"start": v(-34.06, -52) * mm, "mid": v(-43.76, -42.22) * mm, "end": v(-53.46, -52) * mm});
            skArc(sketch, "E174", {"start": v(-20.48, -52) * mm, "mid": v(-27.27, -45.14) * mm, "end": v(-34.06, -52) * mm});
            skArc(sketch, "E175", {"start": v(-3.01, -52) * mm, "mid": v(-11.74, -43.24) * mm, "end": v(-20.48, -52) * mm});
            skLineSegment(sketch, "E176", {"start": v(-68.99, -52) * mm, "end": v(-63.99, -52) * mm});
            skLineSegment(sketch, "E177", {"start": v(-53.46, -52) * mm, "end": v(-58.46, -52) * mm});
            skLineSegment(sketch, "E178", {"start": v(-53.46, -52) * mm, "end": v(-49.46, -52) * mm});
            skLineSegment(sketch, "E179", {"start": v(-34.06, -52) * mm, "end": v(-38.06, -52) * mm});
            skLineSegment(sketch, "E180", {"start": v(-34.06, -52) * mm, "end": v(-31.06, -52) * mm});
            skLineSegment(sketch, "E181", {"start": v(-20.48, -52) * mm, "end": v(-23.48, -52) * mm});
            skLineSegment(sketch, "E182", {"start": v(-20.48, -52) * mm, "end": v(-15.48, -52) * mm});
            skLineSegment(sketch, "E183", {"start": v(-3.01, -52) * mm, "end": v(-8.01, -52) * mm});
            skLineSegment(sketch, "E184", {"start": v(-86.45, -52) * mm, "end": v(-82.45, -52) * mm});
            skLineSegment(sketch, "E185", {"start": v(-68.99, -52) * mm, "end": v(-72.99, -52) * mm});
            skArc(sketch, "E186", {"start": v(-72.99, -52) * mm, "mid": v(-77.72, -47.16) * mm, "end": v(-82.45, -52) * mm});
            skArc(sketch, "E187", {"start": v(-58.46, -52) * mm, "mid": v(-61.22, -49.25) * mm, "end": v(-63.99, -52) * mm});
            skArc(sketch, "E188", {"start": v(-38.06, -52) * mm, "mid": v(-43.76, -46.17) * mm, "end": v(-49.46, -52) * mm});
            skArc(sketch, "E189", {"start": v(-23.48, -52) * mm, "mid": v(-27.27, -48.13) * mm, "end": v(-31.06, -52) * mm});
            skArc(sketch, "E190", {"start": v(-8.01, -52) * mm, "mid": v(-11.74, -48.23) * mm, "end": v(-15.48, -52) * mm});
            const initialGuessF18  = {"E170": [0.00196, -0.05001, 1, 0, 0.00932]};
            skSetInitialGuess(sketch, initialGuessF18);
            skSolve(sketch);
        }
        {
            var Q0;
            Q0 = qSketchRegion(id + "F18", true);
            extrude(context, id + "F19", {"entities" : qUnion([Q0]), "operationType" : NewBodyOperationType.REMOVE, "oppositeDirection" : true, "depth" : 3 * mm});
        }
        {
            var Q0;
            Q0=makeQuery(id+"F12.opExtrude","SWEPT_FACE",FACE,{"disambiguationData":[OSD([sQuery(id+"F11.wireOp",EDGE,"E87")])]});
            var sketch = newSketch(context, id + "F20", { "sketchPlane" : qUnion([Q0])});
            skArc(sketch, "E191", {"start": v(28.4, -23.3) * mm, "mid": v(55.5, -21.34) * mm, "end": v(75, -2.4) * mm});
            skArc(sketch, "E192", {"start": v(46.15, -45.72) * mm, "mid": v(41.3, -31.33) * mm, "end": v(28.4, -23.3) * mm});
            skArc(sketch, "E193", {"start": v(52.8, -71.95) * mm, "mid": v(55.75, -57.25) * mm, "end": v(46.15, -45.72) * mm});
            skArc(sketch, "E194", {"start": v(29.55, -92.87) * mm, "mid": v(48.23, -90.24) * mm, "end": v(52.8, -71.95) * mm});
            skArc(sketch, "E195", {"start": v(21.09, -100.31) * mm, "mid": v(26.58, -98.03) * mm, "end": v(29.55, -92.87) * mm});
            skLineSegment(sketch, "E196", {"start": v(21.09, -100.31) * mm, "end": v(75, -100.31) * mm});
            skLineSegment(sketch, "E197", {"start": v(75, -100.31) * mm, "end": v(75, -2.4) * mm});
            skArc(sketch, "E198", {"start": v(-24.23, -73.44) * mm, "mid": v(-22.68, -92.34) * mm, "end": v(-5.48, -100.31) * mm});
            skArc(sketch, "E199", {"start": v(-53.45, -54.02) * mm, "mid": v(-43.18, -70.26) * mm, "end": v(-24.23, -73.44) * mm});
            skArc(sketch, "E200", {"start": v(-90, -16.5) * mm, "mid": v(-79.22, -42.56) * mm, "end": v(-53.45, -54.02) * mm});
            skLineSegment(sketch, "E201", {"start": v(-5.48, -100.31) * mm, "end": v(-90, -100.31) * mm});
            skLineSegment(sketch, "E202", {"start": v(-90, -100.31) * mm, "end": v(-90, -16.5) * mm});
            skSolve(sketch);
        }
        {
            var Q0;
            {var subQ0=sQuery(id+"F20.wireOp",EDGE,"E193");Q0=makeQuery(id+"F20.imprint","IMPRINT",FACE,{"disambiguationData":[TD([[makeQuery(id+"F20.imprint","IMPRINT",EDGE,{"derivedFrom":subQ0}),-1.0]])]});}
            var Q1;
            {var subQ4=sQuery(id+"F20.wireOp",EDGE,"E199");Q1=makeQuery(id+"F20.imprint","IMPRINT",FACE,{"disambiguationData":[TD([[makeQuery(id+"F20.imprint","IMPRINT",EDGE,{"derivedFrom":subQ4}),-1.0]])]});}
            extrude(context, id + "F21", {"entities" : qUnion([Q0, Q1]), "operationType" : NewBodyOperationType.REMOVE, "oppositeDirection" : true, "depth" : 2 * mm});
        }
    });